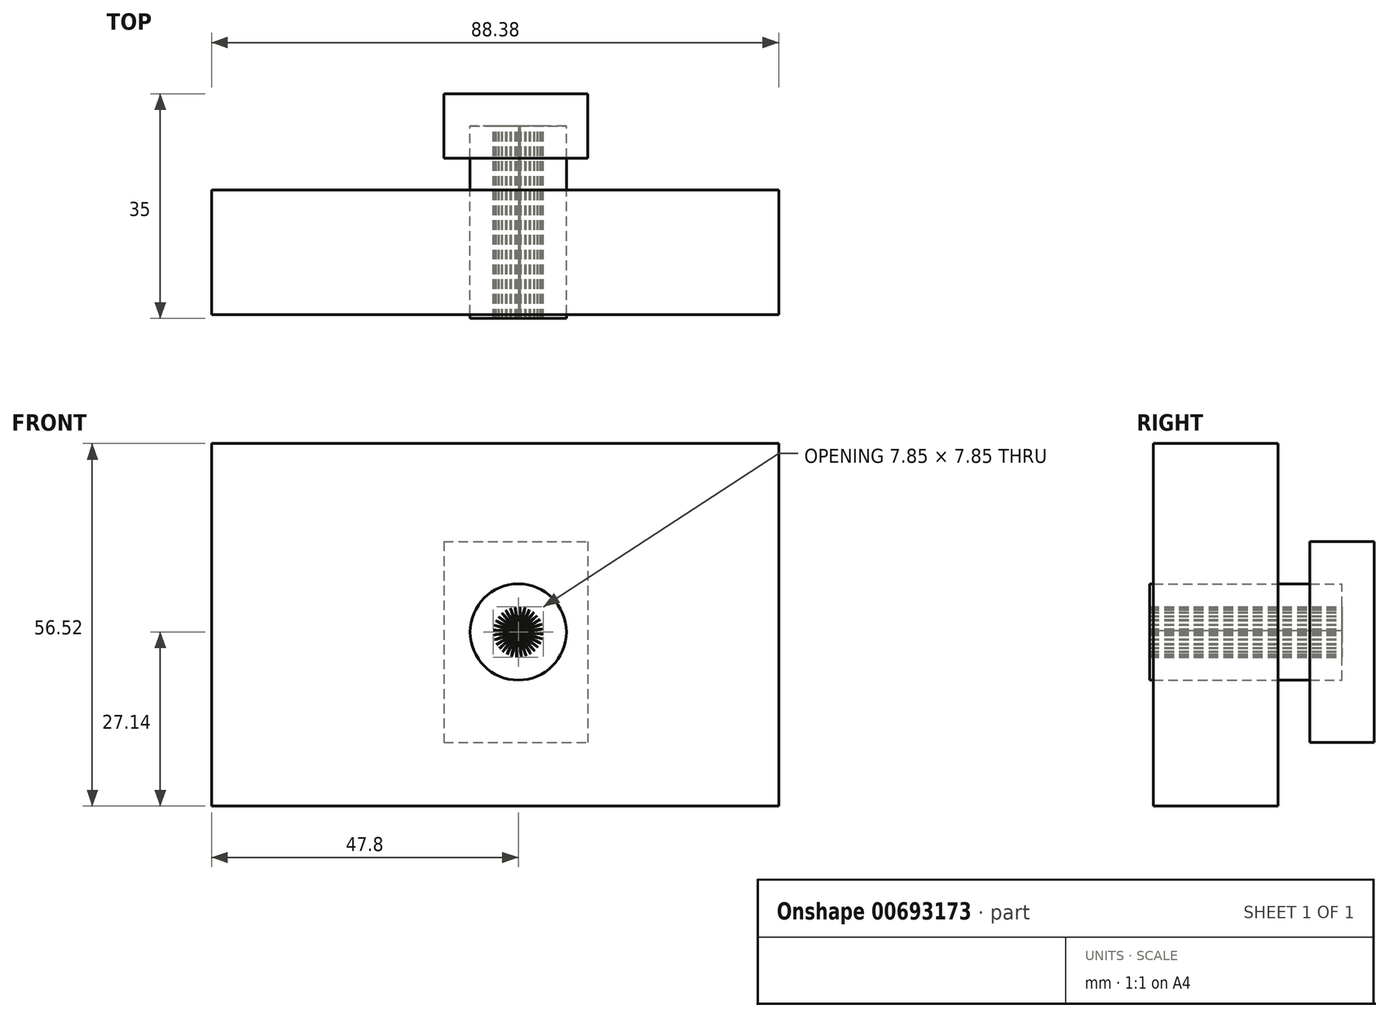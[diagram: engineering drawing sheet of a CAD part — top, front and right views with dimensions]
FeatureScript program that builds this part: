
annotation { "Feature Type Name" : "Feature", "Feature Type Description" : "" }
export const myFeature = defineFeature(function(context is Context, id is Id, definition is map)
    precondition{}
    {
        {
            var Q0;
            Q0=qCreatedBy(makeId("Front.planeOp"),FACE);
            var sketch = newSketch(context, id + "F0", { "sketchPlane" : qUnion([Q0])});
            skFitSpline(sketch, "E0", {"points": [v(-1.67, 7.31) * mm, v(-0.55, 4.2) * mm, v(0, 0.2) * mm, v(0.3, 3.93) * mm, v(0.96, 6.46) * mm, v(1.2, 7.4) * mm], "startDerivative": vector(1.47, -9.38) * mm, "endDerivative": vector(0, 4.87) * mm});
            skCircle(sketch, "E1", {"center": v(0, 0) * mm, "radius": 7.5 * mm});
            skSolve(sketch);
        }
        {
            var Q0;
            {var subQ0=sQuery(id+"F0.wireOp",EDGE,"E0");Q0=makeQuery(id+"F0.imprint","IMPRINT",FACE,{"disambiguationData":[TD([[makeQuery(id+"F0.imprint","IMPRINT",EDGE,{"derivedFrom":subQ0}),1.0]])]});}
            extrude(context, id + "F1", {"entities" : qUnion([Q0]), "depth" : 25 * mm, "offsetDistance" : 25 * mm});
        }
        {
            var Q0;
            Q0=makeQuery(id+"F1.opExtrude","SWEPT_BODY",BODY,{"disambiguationData":[OSD([sQuery(id+"F0.wireOp",EDGE,"E0"),sQuery(id+"F0.wireOp",EDGE,"E1")])]});
            var Q1;
            Q1=sQuery(id+"F0.wireOp",EDGE,"E1");
            circularPattern(context, id + "F2", {"operationType" : NewBodyOperationType.ADD, "entities" : qUnion([Q0]), "axis" : qUnion([Q1]), "angle" : 360 * degree, "instanceCount" : 32, "equalSpace" : true});
        }
        {
            var Q0;
            {var subQ0=makeQuery(id+"F1.opExtrude","CAP_FACE",FACE,{"disambiguationData":[OSD([sQuery(id+"F0.wireOp",EDGE,"E0"),sQuery(id+"F0.wireOp",EDGE,"E1")])],"isStart":true});Q0=makeQuery(id+"F2.boolean.opBoolean","MERGE",FACE,{"derivedFrom":[subQ0,makeQuery(id+"F2.opPattern","COPY",FACE,{"derivedFrom":subQ0,"instanceName":"1"}),makeQuery(id+"F2.opPattern","COPY",FACE,{"derivedFrom":subQ0,"instanceName":"2"}),makeQuery(id+"F2.opPattern","COPY",FACE,{"derivedFrom":subQ0,"instanceName":"3"}),makeQuery(id+"F2.opPattern","COPY",FACE,{"derivedFrom":subQ0,"instanceName":"4"}),makeQuery(id+"F2.opPattern","COPY",FACE,{"derivedFrom":subQ0,"instanceName":"5"}),makeQuery(id+"F2.opPattern","COPY",FACE,{"derivedFrom":subQ0,"instanceName":"6"}),makeQuery(id+"F2.opPattern","COPY",FACE,{"derivedFrom":subQ0,"instanceName":"7"}),makeQuery(id+"F2.opPattern","COPY",FACE,{"derivedFrom":subQ0,"instanceName":"8"}),makeQuery(id+"F2.opPattern","COPY",FACE,{"derivedFrom":subQ0,"instanceName":"9"}),makeQuery(id+"F2.opPattern","COPY",FACE,{"derivedFrom":subQ0,"instanceName":"10"}),makeQuery(id+"F2.opPattern","COPY",FACE,{"derivedFrom":subQ0,"instanceName":"11"}),makeQuery(id+"F2.opPattern","COPY",FACE,{"derivedFrom":subQ0,"instanceName":"12"}),makeQuery(id+"F2.opPattern","COPY",FACE,{"derivedFrom":subQ0,"instanceName":"13"}),makeQuery(id+"F2.opPattern","COPY",FACE,{"derivedFrom":subQ0,"instanceName":"14"}),makeQuery(id+"F2.opPattern","COPY",FACE,{"derivedFrom":subQ0,"instanceName":"15"}),makeQuery(id+"F2.opPattern","COPY",FACE,{"derivedFrom":subQ0,"instanceName":"16"}),makeQuery(id+"F2.opPattern","COPY",FACE,{"derivedFrom":subQ0,"instanceName":"17"}),makeQuery(id+"F2.opPattern","COPY",FACE,{"derivedFrom":subQ0,"instanceName":"18"}),makeQuery(id+"F2.opPattern","COPY",FACE,{"derivedFrom":subQ0,"instanceName":"19"}),makeQuery(id+"F2.opPattern","COPY",FACE,{"derivedFrom":subQ0,"instanceName":"20"}),makeQuery(id+"F2.opPattern","COPY",FACE,{"derivedFrom":subQ0,"instanceName":"21"}),makeQuery(id+"F2.opPattern","COPY",FACE,{"derivedFrom":subQ0,"instanceName":"22"}),makeQuery(id+"F2.opPattern","COPY",FACE,{"derivedFrom":subQ0,"instanceName":"23"}),makeQuery(id+"F2.opPattern","COPY",FACE,{"derivedFrom":subQ0,"instanceName":"24"}),makeQuery(id+"F2.opPattern","COPY",FACE,{"derivedFrom":subQ0,"instanceName":"25"}),makeQuery(id+"F2.opPattern","COPY",FACE,{"derivedFrom":subQ0,"instanceName":"26"}),makeQuery(id+"F2.opPattern","COPY",FACE,{"derivedFrom":subQ0,"instanceName":"27"}),makeQuery(id+"F2.opPattern","COPY",FACE,{"derivedFrom":subQ0,"instanceName":"28"}),makeQuery(id+"F2.opPattern","COPY",FACE,{"derivedFrom":subQ0,"instanceName":"29"}),makeQuery(id+"F2.opPattern","COPY",FACE,{"derivedFrom":subQ0,"instanceName":"30"}),makeQuery(id+"F2.opPattern","COPY",FACE,{"derivedFrom":subQ0,"instanceName":"31"})]});}
            extrude(context, id + "F3", {"entities" : qUnion([Q0]), "operationType" : NewBodyOperationType.ADD, "depth" : 5 * mm, "offsetDistance" : 25 * mm});
        }
        {
            var Q0;
            Q0=qCreatedBy(makeId("Front.planeOp"),FACE);
            var sketch = newSketch(context, id + "F4", { "sketchPlane" : qUnion([Q0])});
            skLineSegment(sketch, "E2.bottom", {"start": v(13.12, -14.04) * mm, "end": v(11.17, -14.04) * mm});
            skLineSegment(sketch, "E2.top", {"start": v(13.12, -10.55) * mm, "end": v(11.17, -10.55) * mm});
            skLineSegment(sketch, "E2.left", {"start": v(13.12, -14.04) * mm, "end": v(13.12, -10.55) * mm});
            skLineSegment(sketch, "E2.right", {"start": v(11.17, -14.04) * mm, "end": v(11.17, -10.55) * mm});
            skLineSegment(sketch, "E3.bottom", {"start": v(-11.61, 14.11) * mm, "end": v(10.82, 14.11) * mm});
            skLineSegment(sketch, "E3.top", {"start": v(-11.61, -17.19) * mm, "end": v(10.82, -17.19) * mm});
            skLineSegment(sketch, "E3.left", {"start": v(-11.61, 14.11) * mm, "end": v(-11.61, -17.19) * mm});
            skLineSegment(sketch, "E3.right", {"start": v(10.82, 14.11) * mm, "end": v(10.82, -17.19) * mm});
            skSolve(sketch);
        }
        {
            var Q0;
            Q0 = qSketchRegion(id + "F4", true);
            var Q1;
            Q1=makeQuery(id+"F4.imprint","IMPRINT",FACE,{"disambiguationData":[TD([[makeQuery(id+"F4.imprint","IMPRINT",EDGE,{"derivedFrom":sQuery(id+"F4.wireOp",EDGE,"E3.bottom")}),-1.0]])]});
            extrude(context, id + "F5", {"entities" : qUnion([Q0, Q1]), "oppositeDirection" : true, "depth" : 10 * mm, "offsetDistance" : 25 * mm});
        }
        {
            var Q0;
            Q0=makeQuery(id+"F5.opExtrude","SWEPT_BODY",BODY,{"disambiguationData":[OSD([sQuery(id+"F4.wireOp",EDGE,"E2.bottom"),sQuery(id+"F4.wireOp",EDGE,"E2.top"),sQuery(id+"F4.wireOp",EDGE,"E2.left"),sQuery(id+"F4.wireOp",EDGE,"E2.right")])]});
            deleteBodies(context, id + "F6", {"entities" : qUnion([Q0])});
        }
        {
            var Q0;
            {var subQ0=makeQuery(id+"F1.opExtrude","CAP_FACE",FACE,{"disambiguationData":[OSD([sQuery(id+"F0.wireOp",EDGE,"E0"),sQuery(id+"F0.wireOp",EDGE,"E1")])],"isStart":false});Q0=makeQuery(id+"F2.boolean.opBoolean","MERGE",FACE,{"derivedFrom":[subQ0,makeQuery(id+"F2.opPattern","COPY",FACE,{"derivedFrom":subQ0,"instanceName":"1"}),makeQuery(id+"F2.opPattern","COPY",FACE,{"derivedFrom":subQ0,"instanceName":"2"}),makeQuery(id+"F2.opPattern","COPY",FACE,{"derivedFrom":subQ0,"instanceName":"3"}),makeQuery(id+"F2.opPattern","COPY",FACE,{"derivedFrom":subQ0,"instanceName":"4"}),makeQuery(id+"F2.opPattern","COPY",FACE,{"derivedFrom":subQ0,"instanceName":"5"}),makeQuery(id+"F2.opPattern","COPY",FACE,{"derivedFrom":subQ0,"instanceName":"6"}),makeQuery(id+"F2.opPattern","COPY",FACE,{"derivedFrom":subQ0,"instanceName":"7"}),makeQuery(id+"F2.opPattern","COPY",FACE,{"derivedFrom":subQ0,"instanceName":"8"}),makeQuery(id+"F2.opPattern","COPY",FACE,{"derivedFrom":subQ0,"instanceName":"9"}),makeQuery(id+"F2.opPattern","COPY",FACE,{"derivedFrom":subQ0,"instanceName":"10"}),makeQuery(id+"F2.opPattern","COPY",FACE,{"derivedFrom":subQ0,"instanceName":"11"}),makeQuery(id+"F2.opPattern","COPY",FACE,{"derivedFrom":subQ0,"instanceName":"12"}),makeQuery(id+"F2.opPattern","COPY",FACE,{"derivedFrom":subQ0,"instanceName":"13"}),makeQuery(id+"F2.opPattern","COPY",FACE,{"derivedFrom":subQ0,"instanceName":"14"}),makeQuery(id+"F2.opPattern","COPY",FACE,{"derivedFrom":subQ0,"instanceName":"15"}),makeQuery(id+"F2.opPattern","COPY",FACE,{"derivedFrom":subQ0,"instanceName":"16"}),makeQuery(id+"F2.opPattern","COPY",FACE,{"derivedFrom":subQ0,"instanceName":"17"}),makeQuery(id+"F2.opPattern","COPY",FACE,{"derivedFrom":subQ0,"instanceName":"18"}),makeQuery(id+"F2.opPattern","COPY",FACE,{"derivedFrom":subQ0,"instanceName":"19"}),makeQuery(id+"F2.opPattern","COPY",FACE,{"derivedFrom":subQ0,"instanceName":"20"}),makeQuery(id+"F2.opPattern","COPY",FACE,{"derivedFrom":subQ0,"instanceName":"21"}),makeQuery(id+"F2.opPattern","COPY",FACE,{"derivedFrom":subQ0,"instanceName":"22"}),makeQuery(id+"F2.opPattern","COPY",FACE,{"derivedFrom":subQ0,"instanceName":"23"}),makeQuery(id+"F2.opPattern","COPY",FACE,{"derivedFrom":subQ0,"instanceName":"24"}),makeQuery(id+"F2.opPattern","COPY",FACE,{"derivedFrom":subQ0,"instanceName":"25"}),makeQuery(id+"F2.opPattern","COPY",FACE,{"derivedFrom":subQ0,"instanceName":"26"}),makeQuery(id+"F2.opPattern","COPY",FACE,{"derivedFrom":subQ0,"instanceName":"27"}),makeQuery(id+"F2.opPattern","COPY",FACE,{"derivedFrom":subQ0,"instanceName":"28"}),makeQuery(id+"F2.opPattern","COPY",FACE,{"derivedFrom":subQ0,"instanceName":"29"}),makeQuery(id+"F2.opPattern","COPY",FACE,{"derivedFrom":subQ0,"instanceName":"30"}),makeQuery(id+"F2.opPattern","COPY",FACE,{"derivedFrom":subQ0,"instanceName":"31"})]});}
            cPlane(context, id + "F7", {"entities" : qUnion([Q0]), "cplaneType" : CPlaneType.OFFSET, "offset" : 0.6 * mm, "oppositeDirection" : true, "width" : 150 * mm, "height" : 150 * mm});
        }
        {
            var Q0;
            Q0=qCreatedBy(id+"F7.planeOp",FACE);
            var sketch = newSketch(context, id + "F8", { "sketchPlane" : qUnion([Q0])});
            skLineSegment(sketch, "E4.bottom", {"start": v(40.58, -27.14) * mm, "end": v(-47.8, -27.14) * mm});
            skLineSegment(sketch, "E4.top", {"start": v(40.58, 29.38) * mm, "end": v(-47.8, 29.38) * mm});
            skLineSegment(sketch, "E4.left", {"start": v(40.58, -27.14) * mm, "end": v(40.58, 29.38) * mm});
            skLineSegment(sketch, "E4.right", {"start": v(-47.8, -27.14) * mm, "end": v(-47.8, 29.38) * mm});
            skSolve(sketch);
        }
        {
            var Q0;
            Q0=makeQuery(id+"F8.imprint","IMPRINT",FACE,{"disambiguationData":[TD([[makeQuery(id+"F8.imprint","IMPRINT",EDGE,{"derivedFrom":sQuery(id+"F8.wireOp",EDGE,"E4.bottom")}),-1.0]])]});
            extrude(context, id + "F9", {"entities" : qUnion([Q0]), "oppositeDirection" : true, "depth" : 19.4 * mm, "offsetDistance" : 25 * mm});
        }
    });
